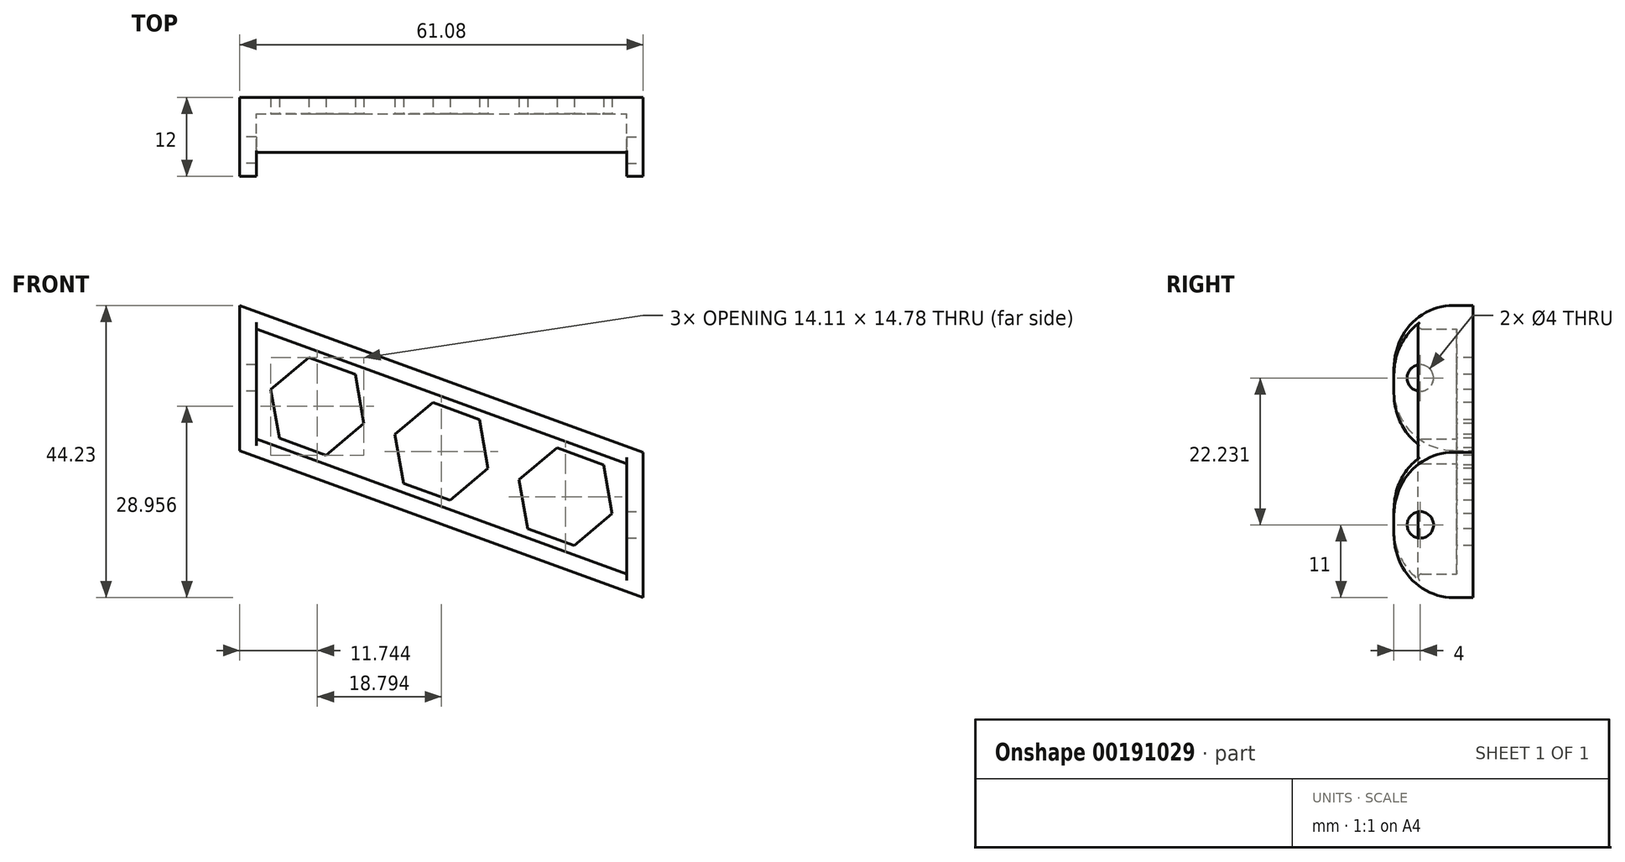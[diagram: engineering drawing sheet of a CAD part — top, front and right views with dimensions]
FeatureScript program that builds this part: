
annotation { "Feature Type Name" : "Feature", "Feature Type Description" : "" }
export const myFeature = defineFeature(function(context is Context, id is Id, definition is map)
    precondition{}
    {
        {
            var Q0;
            Q0=qCreatedBy(makeId("Front.planeOp"),FACE);
            var sketch = newSketch(context, id + "F0", { "sketchPlane" : qUnion([Q0])});
            skLineSegment(sketch, "E0", {"start": v(-21.6, 22.23) * mm, "end": v(39.49, 0) * mm});
            skLineSegment(sketch, "E1", {"start": v(39.49, 0) * mm, "end": v(39.49, -22) * mm});
            skLineSegment(sketch, "E2", {"start": v(39.49, -22) * mm, "end": v(-21.6, 0.23) * mm});
            skLineSegment(sketch, "E3", {"start": v(-21.6, 0.23) * mm, "end": v(-21.6, 22.23) * mm});
            skLineSegment(sketch, "E4", {"start": v(-37.67, -46.26) * mm, "end": v(59.8, -46.26) * mm, "construction": true});
            skLineSegment(sketch, "E5", {"start": v(77.46, 10.71) * mm, "end": v(77.46, -42.73) * mm, "construction": true});
            skSolve(sketch);
        }
        {
            var Q0;
            Q0=makeQuery(id+"F0.imprint","IMPRINT",FACE,{"disambiguationData":[TD([[makeQuery(id+"F0.imprint","IMPRINT",EDGE,{"derivedFrom":sQuery(id+"F0.wireOp",EDGE,"E0")}),-1.0]])]});
            extrude(context, id + "F1", {"entities" : qUnion([Q0]), "depth" : 12 * mm});
        }
        {
            var Q0;
            Q0=makeQuery(id+"F1.opExtrude","CAP_FACE",FACE,{"disambiguationData":[OSD([sQuery(id+"F0.wireOp",EDGE,"E0"),sQuery(id+"F0.wireOp",EDGE,"E1"),sQuery(id+"F0.wireOp",EDGE,"E2"),sQuery(id+"F0.wireOp",EDGE,"E3")])],"isStart":false});
            shell(context, id + "F2", {"entities" : qUnion([Q0]), "thickness" : 2.5 * mm});
        }
        {
            var Q0;
            Q0=makeQuery(id+"F1.opExtrude","SWEPT_FACE",FACE,{"disambiguationData":[OSD([sQuery(id+"F0.wireOp",EDGE,"E3")])]});
            var sketch = newSketch(context, id + "F3", { "sketchPlane" : qUnion([Q0])});
            skPoint(sketch, "E6", {"position": v(8, 11.23) * mm});
            skLineSegment(sketch, "E7", {"start": v(0, 11.23) * mm, "end": v(12, 11.23) * mm, "construction": true});
            skLineSegment(sketch, "E8.bottom", {"start": v(0, 22.23) * mm, "end": v(12, 22.23) * mm});
            skLineSegment(sketch, "E8.top", {"start": v(0, 0.23) * mm, "end": v(12, 0.23) * mm});
            skLineSegment(sketch, "E8.left", {"start": v(0, 22.23) * mm, "end": v(0, 0.23) * mm});
            skLineSegment(sketch, "E8.right", {"start": v(12, 22.23) * mm, "end": v(12, 0.23) * mm});
            skSolve(sketch);
        }
        {
            var Q0;
            Q0=sQuery(id+"F3.wireOp",VERTEX,"E6");
            var Q1;
            Q1=makeQuery(id+"F1.opExtrude","SWEPT_BODY",BODY,{"disambiguationData":[OSD([sQuery(id+"F0.wireOp",EDGE,"E0"),sQuery(id+"F0.wireOp",EDGE,"E1"),sQuery(id+"F0.wireOp",EDGE,"E2"),sQuery(id+"F0.wireOp",EDGE,"E3")])]});
            hole(context, id + "F4", {"style" : HoleStyle.SIMPLE, "endStyle" : HoleEndStyle.BLIND, "holeDiameter" : 4 * mm, "holeDepth" : 6 * mm, "locations" : qUnion([Q0]), "scope" : qUnion([Q1])});
        }
        {
            var Q0;
            Q0=makeQuery(id+"F1.opExtrude","SWEPT_FACE",FACE,{"disambiguationData":[OSD([sQuery(id+"F0.wireOp",EDGE,"E1")])]});
            var sketch = newSketch(context, id + "F5", { "sketchPlane" : qUnion([Q0])});
            skPoint(sketch, "E9", {"position": v(-8, -11) * mm});
            skLineSegment(sketch, "E10", {"start": v(-12, -11) * mm, "end": v(0, -11) * mm, "construction": true});
            skSolve(sketch);
        }
        {
            var Q0;
            Q0=sQuery(id+"F5.wireOp",VERTEX,"E9");
            var Q1;
            Q1=makeQuery(id+"F1.opExtrude","SWEPT_BODY",BODY,{"disambiguationData":[OSD([sQuery(id+"F0.wireOp",EDGE,"E0"),sQuery(id+"F0.wireOp",EDGE,"E1"),sQuery(id+"F0.wireOp",EDGE,"E2"),sQuery(id+"F0.wireOp",EDGE,"E3")])]});
            hole(context, id + "F6", {"style" : HoleStyle.SIMPLE, "endStyle" : HoleEndStyle.BLIND, "holeDiameter" : 4 * mm, "holeDepth" : 6 * mm, "locations" : qUnion([Q0]), "scope" : qUnion([Q1])});
        }
        {
            var Q0;
            Q0=makeQuery(id+"F1.opExtrude","CAP_EDGE",EDGE,{"disambiguationData":[OSD([sQuery(id+"F0.wireOp",EDGE,"E0")])],"isStart":false});
            var Q1;
            Q1=makeQuery(id+"F1.opExtrude","CAP_EDGE",EDGE,{"disambiguationData":[OSD([sQuery(id+"F0.wireOp",EDGE,"E2")])],"isStart":false});
            fillet(context, id + "F7", {"entities" : qUnion([Q0, Q1]), "radius" : 9 * mm, "tangentPropagation" : true, "allowEdgeOverflow" : false});
        }
        {
            var Q0;
            Q0=makeQuery(id+"F2.opShell","OFFSET_FACE",FACE,{"disambiguationData":[OSD([sQuery(id+"F0.wireOp",EDGE,"E0"),sQuery(id+"F0.wireOp",EDGE,"E1"),sQuery(id+"F0.wireOp",EDGE,"E2"),sQuery(id+"F0.wireOp",EDGE,"E3")])]});
            var sketch = newSketch(context, id + "F8", { "sketchPlane" : qUnion([Q0])});
            skCircle(sketch, "E11.cCircle", {"center": v(-9.85, 6.96) * mm, "radius": 6.5 * mm, "construction": true});
            skLineSegment(sketch, "E11.0", {"start": v(-2.8, 4.39) * mm, "end": v(-8.54, -0.44) * mm});
            skLineSegment(sketch, "E11.1", {"start": v(-8.54, -0.44) * mm, "end": v(-15.6, 2.13) * mm});
            skLineSegment(sketch, "E11.2", {"start": v(-15.6, 2.13) * mm, "end": v(-16.9, 9.52) * mm});
            skLineSegment(sketch, "E11.3", {"start": v(-16.9, 9.52) * mm, "end": v(-11.15, 14.35) * mm});
            skLineSegment(sketch, "E11.4", {"start": v(-11.15, 14.35) * mm, "end": v(-4.1, 11.78) * mm});
            skLineSegment(sketch, "E11.5", {"start": v(-4.1, 11.78) * mm, "end": v(-2.8, 4.39) * mm});
            skPoint(sketch, "E11.0.midPoint", {"position": v(-5.67, 1.98) * mm});
            skLineSegment(sketch, "E12", {"start": v(8.95, 0.12) * mm, "end": v(-19.1, 10.32) * mm, "construction": true});
            skCircle(sketch, "E13.cCircle", {"center": v(8.95, 0.12) * mm, "radius": 6.5 * mm, "construction": true});
            skLineSegment(sketch, "E13.0", {"start": v(16, -2.45) * mm, "end": v(10.25, -7.28) * mm});
            skLineSegment(sketch, "E13.1", {"start": v(10.25, -7.28) * mm, "end": v(3.2, -4.7) * mm});
            skLineSegment(sketch, "E13.2", {"start": v(3.2, -4.7) * mm, "end": v(1.9, 2.68) * mm});
            skLineSegment(sketch, "E13.3", {"start": v(1.9, 2.68) * mm, "end": v(7.64, 7.5) * mm});
            skLineSegment(sketch, "E13.4", {"start": v(7.64, 7.5) * mm, "end": v(14.7, 4.94) * mm});
            skLineSegment(sketch, "E13.5", {"start": v(14.7, 4.94) * mm, "end": v(16, -2.45) * mm});
            skCircle(sketch, "E14.cCircle", {"center": v(27.74, -6.72) * mm, "radius": 6.5 * mm, "construction": true});
            skLineSegment(sketch, "E14.0", {"start": v(34.8, -9.3) * mm, "end": v(29.04, -14.12) * mm});
            skLineSegment(sketch, "E14.1", {"start": v(29.04, -14.12) * mm, "end": v(22, -11.55) * mm});
            skLineSegment(sketch, "E14.2", {"start": v(22, -11.55) * mm, "end": v(20.69, -4.16) * mm});
            skLineSegment(sketch, "E14.3", {"start": v(20.69, -4.16) * mm, "end": v(26.44, 0.67) * mm});
            skLineSegment(sketch, "E14.4", {"start": v(26.44, 0.67) * mm, "end": v(33.5, -1.9) * mm});
            skLineSegment(sketch, "E14.5", {"start": v(33.5, -1.9) * mm, "end": v(34.8, -9.3) * mm});
            skLineSegment(sketch, "E15", {"start": v(8.95, 0.12) * mm, "end": v(36.99, -10.1) * mm, "construction": true});
            skLineSegment(sketch, "E16", {"start": v(8.95, 8.46) * mm, "end": v(8.95, -8.22) * mm, "construction": true});
            skSolve(sketch);
        }
        {
            var Q0;
            Q0=makeQuery(id+"F8.imprint","IMPRINT",FACE,{"disambiguationData":[TD([[makeQuery(id+"F8.imprint","IMPRINT",EDGE,{"derivedFrom":sQuery(id+"F8.wireOp",EDGE,"E11.0")}),-1.0]])]});
            var Q1;
            Q1=makeQuery(id+"F8.imprint","IMPRINT",FACE,{"disambiguationData":[TD([[makeQuery(id+"F8.imprint","IMPRINT",EDGE,{"derivedFrom":sQuery(id+"F8.wireOp",EDGE,"E13.0")}),-1.0]])]});
            var Q2;
            Q2=makeQuery(id+"F8.imprint","IMPRINT",FACE,{"disambiguationData":[TD([[makeQuery(id+"F8.imprint","IMPRINT",EDGE,{"derivedFrom":sQuery(id+"F8.wireOp",EDGE,"E14.0")}),-1.0]])]});
            extrude(context, id + "F9", {"entities" : qUnion([Q0, Q1, Q2]), "operationType" : NewBodyOperationType.REMOVE, "oppositeDirection" : true, "depth" : 25 * mm});
        }
        {
            var Q0;
            {var subQ0=sQuery(id+"F0.wireOp",EDGE,"E2");Q0=makeQuery(id+"F7.opFillet","BLEND_EDGE",EDGE,{"blendedFrom":[makeQuery(id+"F1.opExtrude","CAP_EDGE",EDGE,{"disambiguationData":[OSD([subQ0])],"isStart":false}),makeQuery(id+"F2.opShell","OFFSET_FACE",FACE,{"disambiguationData":[OSD([subQ0])]})],"blendedInto":[makeQuery(id+"F2.opShell","OFFSET_FACE",FACE,{"disambiguationData":[OSD([subQ0])]})]});}
            var Q1;
            {var subQ0=sQuery(id+"F0.wireOp",EDGE,"E0");Q1=makeQuery(id+"F7.opFillet","BLEND_EDGE",EDGE,{"blendedFrom":[makeQuery(id+"F1.opExtrude","CAP_EDGE",EDGE,{"disambiguationData":[OSD([subQ0])],"isStart":false}),makeQuery(id+"F2.opShell","OFFSET_FACE",FACE,{"disambiguationData":[OSD([subQ0])]})],"blendedInto":[makeQuery(id+"F2.opShell","OFFSET_FACE",FACE,{"disambiguationData":[OSD([subQ0])]})]});}
            fillet(context, id + "F10", {"entities" : qUnion([Q0, Q1]), "radius" : .5 * mm, "tangentPropagation" : true, "allowEdgeOverflow" : false});
        }
    });
